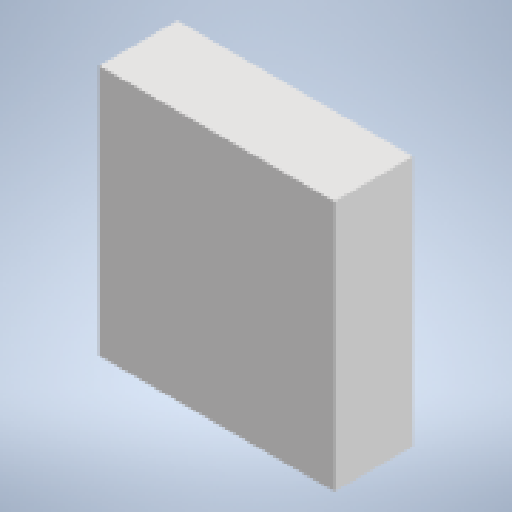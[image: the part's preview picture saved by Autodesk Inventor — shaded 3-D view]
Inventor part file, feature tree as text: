
AUTODESK INVENTOR PART (.ipt)
format: ipt  version: 2025 (Build 290162010, 162A)  size: 112,128 bytes
history: native  units: mm
features: extrude x1, sketch x1
ambient origin geometry x8: Origin, YZ Plane, XZ Plane, XY Plane, X Axis, Y Axis, Z Axis, Center Point
bodies: Volumenkörper1 (feature_tree)
feature tree (2):
  extrude  "Extrusion1"  Depth=32.0mm
  sketch  "Skizze1"  dims[d0=30.0mm d1=32.0mm d2=10.0mm d3=0.0mm]
